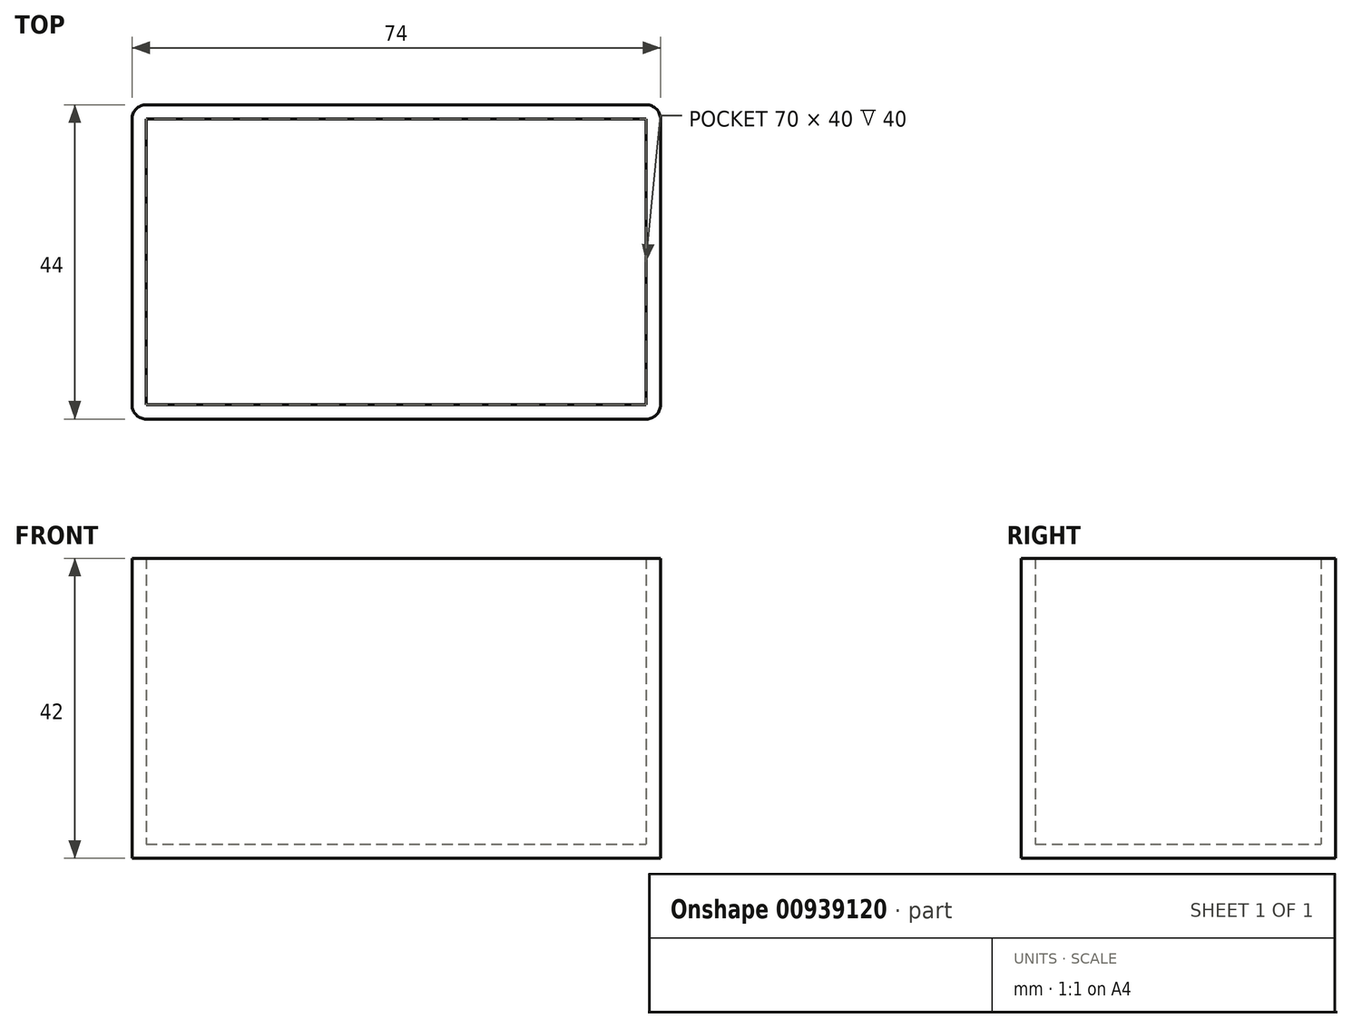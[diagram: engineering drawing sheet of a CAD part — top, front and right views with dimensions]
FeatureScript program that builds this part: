
annotation { "Feature Type Name" : "Feature", "Feature Type Description" : "" }
export const myFeature = defineFeature(function(context is Context, id is Id, definition is map)
    precondition{}
    {
        {
            var Q0;
            Q0=qCreatedBy(makeId("Top.planeOp"),FACE);
            var sketch = newSketch(context, id + "F0", { "sketchPlane" : qUnion([Q0])});
            skLineSegment(sketch, "E0.bottom", {"start": v(-35, -20) * mm, "end": v(35, -20) * mm});
            skLineSegment(sketch, "E0.top", {"start": v(-35, 20) * mm, "end": v(35, 20) * mm});
            skLineSegment(sketch, "E0.left", {"start": v(-35, -20) * mm, "end": v(-35, 20) * mm});
            skLineSegment(sketch, "E0.right", {"start": v(35, -20) * mm, "end": v(35, 20) * mm});
            skPoint(sketch, "E0.middle", {"position": v(0, 0) * mm});
            skLineSegment(sketch, "E1.bottom", {"start": v(-35, 20) * mm, "end": v(-37, 20) * mm});
            skLineSegment(sketch, "E1.top", {"start": v(-35, -20) * mm, "end": v(-37, -20) * mm});
            skLineSegment(sketch, "E1.left", {"start": v(-35, 20) * mm, "end": v(-35, -20) * mm});
            skLineSegment(sketch, "E1.right", {"start": v(-37, 20) * mm, "end": v(-37, -20) * mm});
            skLineSegment(sketch, "E2", {"start": v(0, 20) * mm, "end": v(0, -20) * mm, "construction": true});
            skLineSegment(sketch, "E3.MirrorCS", {"start": v(37, 20) * mm, "end": v(37, -20) * mm});
            skLineSegment(sketch, "E4.MirrorCS", {"start": v(35, -20) * mm, "end": v(37, -20) * mm});
            skLineSegment(sketch, "E5", {"start": v(35, 20) * mm, "end": v(37, 20) * mm, "construction": true});
            skLineSegment(sketch, "E6", {"start": v(35, 20) * mm, "end": v(37, 20) * mm});
            skLineSegment(sketch, "E7.bottom", {"start": v(-37, 20) * mm, "end": v(37, 20) * mm});
            skLineSegment(sketch, "E7.top", {"start": v(-37, 22) * mm, "end": v(37, 22) * mm});
            skLineSegment(sketch, "E7.left", {"start": v(-37, 20) * mm, "end": v(-37, 22) * mm});
            skLineSegment(sketch, "E7.right", {"start": v(37, 20) * mm, "end": v(37, 22) * mm});
            skLineSegment(sketch, "E8", {"start": v(-37, 0) * mm, "end": v(37, 0) * mm, "construction": true});
            skLineSegment(sketch, "E9.MirrorCS", {"start": v(-37, -22) * mm, "end": v(37, -22) * mm});
            skLineSegment(sketch, "E10.MirrorCS", {"start": v(37, -20) * mm, "end": v(37, -22) * mm});
            skLineSegment(sketch, "E11", {"start": v(-37, -20) * mm, "end": v(-37, -22) * mm});
            skSolve(sketch);
        }
        {
            var Q0;
            Q0=makeQuery(id+"F0.imprint","IMPRINT",FACE,{"disambiguationData":[TD([[makeQuery(id+"F0.imprint","IMPRINT",EDGE,{"derivedFrom":sQuery(id+"F0.wireOp",EDGE,"E7.top")}),-1.0]])]});
            var Q1;
            Q1=makeQuery(id+"F0.imprint","IMPRINT",FACE,{"disambiguationData":[TD([[makeQuery(id+"F0.imprint","IMPRINT",EDGE,{"derivedFrom":sQuery(id+"F0.wireOp",EDGE,"E1.top")}),-1.0]])]});
            var Q2;
            Q2=makeQuery(id+"F0.imprint","IMPRINT",FACE,{"disambiguationData":[TD([[makeQuery(id+"F0.imprint","IMPRINT",EDGE,{"derivedFrom":sQuery(id+"F0.wireOp",EDGE,"E0.bottom")}),-1.0]])]});
            var Q3;
            {var subQ0=sQuery(id+"F0.wireOp",EDGE,"E0.right");Q3=makeQuery(id+"F0.imprint","IMPRINT",FACE,{"disambiguationData":[TD([[makeQuery(id+"F0.imprint","IMPRINT",EDGE,{"derivedFrom":subQ0}),-1.0]])]});}
            extrude(context, id + "F1", {"entities" : qUnion([Q0, Q1, Q2, Q3]), "depth" : 42 * mm, "offsetDistance" : 25 * mm});
        }
        {
            var Q0;
            Q0=makeQuery(id+"F1.opExtrude","CAP_FACE",FACE,{"disambiguationData":[OSD([sQuery(id+"F0.wireOp",EDGE,"E0.bottom"),sQuery(id+"F0.wireOp",EDGE,"E0.right"),sQuery(id+"F0.wireOp",EDGE,"E1.left"),sQuery(id+"F0.wireOp",EDGE,"E1.right"),sQuery(id+"F0.wireOp",EDGE,"E3.MirrorCS"),sQuery(id+"F0.wireOp",EDGE,"E7.bottom"),sQuery(id+"F0.wireOp",EDGE,"E7.top"),sQuery(id+"F0.wireOp",EDGE,"E7.left"),sQuery(id+"F0.wireOp",EDGE,"E7.right"),sQuery(id+"F0.wireOp",EDGE,"E9.MirrorCS"),sQuery(id+"F0.wireOp",EDGE,"E10.MirrorCS"),sQuery(id+"F0.wireOp",EDGE,"E11")])],"isStart":true});
            var sketch = newSketch(context, id + "F2", { "sketchPlane" : qUnion([Q0])});
            skLineSegment(sketch, "E12.bottom", {"start": v(-35, 20) * mm, "end": v(35, 20) * mm});
            skLineSegment(sketch, "E12.top", {"start": v(-35, -20) * mm, "end": v(35, -20) * mm});
            skLineSegment(sketch, "E12.left", {"start": v(-35, 20) * mm, "end": v(-35, -20) * mm});
            skLineSegment(sketch, "E12.right", {"start": v(35, 20) * mm, "end": v(35, -20) * mm});
            skPoint(sketch, "E12.middle", {"position": v(0, 0) * mm});
            skSolve(sketch);
        }
        {
            var Q0;
            Q0 = qSketchRegion(id + "F2", true);
            extrude(context, id + "F3", {"entities" : qUnion([Q0]), "operationType" : NewBodyOperationType.ADD, "oppositeDirection" : true, "depth" : 2 * mm, "offsetDistance" : 25 * mm});
        }
        {
            var Q0;
            Q0=makeQuery(id+"F1.opExtrude","SWEPT_EDGE",EDGE,{"disambiguationData":[OSD([sQuery(id+"F0.wireOp",EDGE,"E9.MirrorCS"),sQuery(id+"F0.wireOp",EDGE,"E10.MirrorCS")])]});
            var Q1;
            Q1=makeQuery(id+"F1.opExtrude","SWEPT_EDGE",EDGE,{"disambiguationData":[OSD([sQuery(id+"F0.wireOp",EDGE,"E7.top"),sQuery(id+"F0.wireOp",EDGE,"E7.right")])]});
            var Q2;
            Q2=makeQuery(id+"F1.opExtrude","SWEPT_EDGE",EDGE,{"disambiguationData":[OSD([sQuery(id+"F0.wireOp",EDGE,"E9.MirrorCS"),sQuery(id+"F0.wireOp",EDGE,"E11")])]});
            var Q3;
            Q3=makeQuery(id+"F1.opExtrude","SWEPT_EDGE",EDGE,{"disambiguationData":[OSD([sQuery(id+"F0.wireOp",EDGE,"E7.top"),sQuery(id+"F0.wireOp",EDGE,"E7.left")])]});
            fillet(context, id + "F4", {"entities" : qUnion([Q0, Q1, Q2, Q3]), "radius" : 2 * mm, "tangentPropagation" : true, "allowEdgeOverflow" : false});
        }
    });
